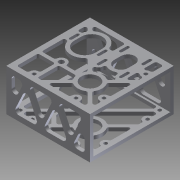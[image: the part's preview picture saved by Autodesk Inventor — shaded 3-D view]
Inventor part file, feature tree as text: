
AUTODESK INVENTOR PART (.ipt)
format: ipt  version: 2012 (Build 160160000, 160)  size: 865,792 bytes
history: native  units: in
note: dims shown in document units (in); Inventor stores cm internally (conversion verified against a paired STEP export)
features: extrude x7, sketch x5, fillet x3, projected_geometry x1
ambient origin geometry x8: Origin, YZ Plane, XZ Plane, XY Plane, X Axis, Y Axis, Z Axis, Center Point
bodies: Solid1 (feature_tree)
feature tree (16):
  extrude  "Extrusion1"  Depth=0.1875in
  sketch  "Sketch2"  dims[d4=0.25in d5=0.25in d6=6.0in d7=0.0in]
  extrude  "Extrusion2"  Depth=6.0in TaperAngle=0.0deg
  extrude  "Extrusion3"  Depth=1.25in
  extrude  "Extrusion4"  Depth=1.625in
  fillet  "Fillet2"  Radius=0.375in
  sketch  "Sketch6"  dims[d20=0.25in d21=0.125in d22=0.25in d24=0.25in d25=0.125in d27=0.125in d32=0.25in d33=0.0in d35=0.375in d36=0.375in d37=0.375in d38=0.375in d39=0.1719in d40=0.3438in d41=0.3438in d42=0.3438in d43=0.3438in d44=0.125in d46=0.125in d49=0.125in d50=0.125in d51=0.125in d52=0.125in d53=0.125in d54=0.125in d55=0.125in d56=0.125in d57=0.25in d58=0.0in d59=0.1719in d60=0.3438in d61=0.3438in d62=0.3438in d63=0.3438in d64=0.125in d65=0.125in d66=0.125in d67=0.125in d68=0.125in d69=0.125in d70=0.125in d71=0.125in d72=0.125in d73=0.125in d74=0.375in d76=0.375in d77=0.375in d78=0.375in d79=0.25in d80=0.0in d81=0.25in d88=0.125in d89=1.25in d90=1.5in d91=0.75in d92=0.5in d94=0.2in d96=0.9in d97=1.0in d98=0.5in d99=0.5in d101=2.0in d102=0.2in d103=0.8in d104=0.8in d105=0.7874in d107=1.6in d108=0.7874in d110=1.6in d114=1.0in d115=1.0in d116=1.625in d117=1.0in d119=0.2in d122=4.5in d123=1.3125in d124=0.366in d126=2.3in d127=0.25in d128=0.0in d129=0.375in d131=4.5in d132=0.125in d153=0.25in d154=0.125in d156=0.375in d157=0.375in d160=0.25in d161=0.125in d162=0.25in d163=0.125in d165=0.875in d166=0.125in d168=0.375in d169=0.25in d170=0.125in d171=1.0in d172=0.25in d177=0.125in d178=0.6in d179=0.25in d180=0.0in d181=0.125in d183=0.25in d185=0.25in d186=0.125in d188=1.5625in d190=1.3125in d191=0.366in d193=0.25in d194=0.125in d197=1.0in d198=1.176in d199=0.1in d200=0.0in d201=0.125in d203=0.25in d204=0.25in d205=0.125in d207=2.1875in d208=2.0312in d211=0.125in d212=0.3in d213=0.5in d214=0.25in d215=0.3125in d220=0.5in d221=1.5in d222=0.25in d224=0.1875in d225=2.3in d226=0.35in d227=0.25in d228=1.5in d229=1.5in d230=0.5821in d231=0.25in d232=1.5in d233=0.125in d234=0.25in d235=2.0in d236=0.25in d237=1.5in d238=0.3125in d239=0.7874in d241=3.0in d242=0.3937in d244=1.0in d246=1.5in d247=0.7874in d249=3.0in d250=0.3937in d252=1.0in d254=0.5in d255=0.25in d256=0.3125in d257=0.25in d258=0.5in d259=0.3125in d260=0.25in d262=0.75in d264=6.0in d267=0.25in d269=3.0in d270=6.0in d272=0.25in]
  fillet  "Fillet3"  Radius=0.875in
  extrude  "Extrusion5"  Depth=0.125in
  extrude  "Extrusion6"  Depth=0.25in
  fillet  "Fillet4"  Radius=0.25in
  extrude  "Extrusion7"  Depth=0.125in
  sketch  "Sketch1"  dims[d1=3.0in d2=0.1875in d3=0.25in]
  sketch  "Sketch4"  dims[d11=2.0312in d13=1.25in]
  sketch  "Sketch5"  dims[d15=2.625in d16=1.625in d18=0.375in d19=0.875in]
  projected_geometry  "Projected Loop1"
